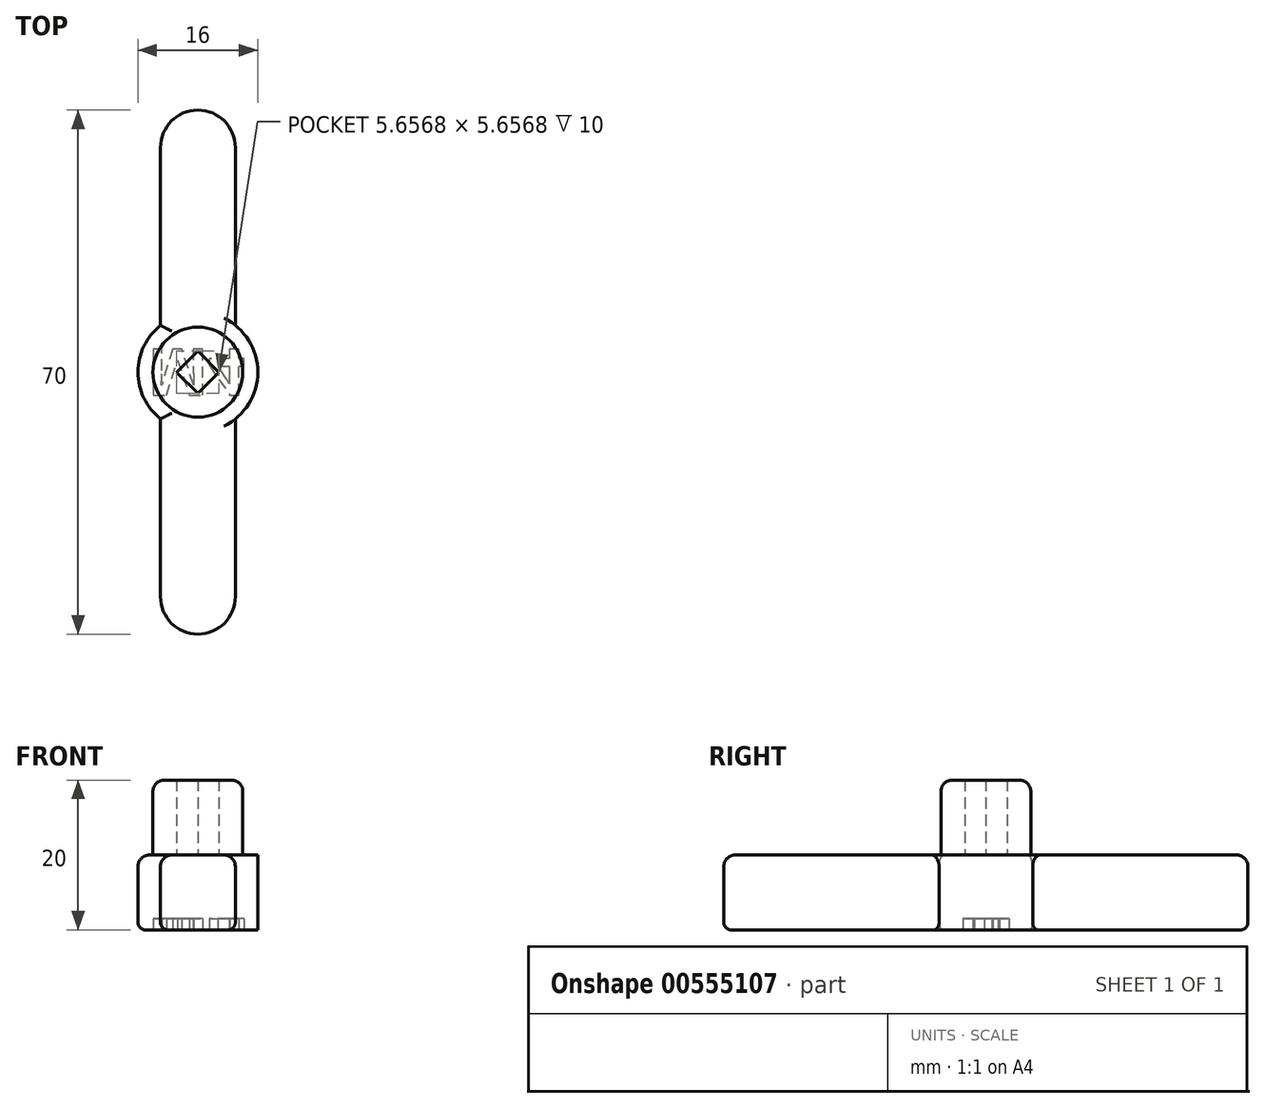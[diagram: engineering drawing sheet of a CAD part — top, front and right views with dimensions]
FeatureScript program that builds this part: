
annotation { "Feature Type Name" : "Feature", "Feature Type Description" : "" }
export const myFeature = defineFeature(function(context is Context, id is Id, definition is map)
    precondition{}
    {
        {
            var Q0;
            Q0=qCreatedBy(makeId("Top.planeOp"),FACE);
            var sketch = newSketch(context, id + "F0", { "sketchPlane" : qUnion([Q0])});
            skLineSegment(sketch, "E0.bottom", {"start": v(5, -30) * mm, "end": v(-5, -30) * mm});
            skLineSegment(sketch, "E0.top", {"start": v(5, 30) * mm, "end": v(-5, 30) * mm});
            skLineSegment(sketch, "E0.left", {"start": v(5, -30) * mm, "end": v(5, 30) * mm});
            skLineSegment(sketch, "E0.right", {"start": v(-5, -30) * mm, "end": v(-5, 30) * mm});
            skPoint(sketch, "E0.middle", {"position": v(0, 0) * mm});
            skArc(sketch, "E1", {"start": v(5, 30) * mm, "mid": v(0, 35) * mm, "end": v(-5, 30) * mm});
            skArc(sketch, "E2", {"start": v(-5, -30) * mm, "mid": v(0, -35) * mm, "end": v(5, -30) * mm});
            skCircle(sketch, "E3", {"center": v(0, 0) * mm, "radius": 8 * mm});
            skCircle(sketch, "E4", {"center": v(0, 0) * mm, "radius": 6 * mm});
            skCircle(sketch, "E5.cCircle", {"center": v(0, 0) * mm, "radius": 2.83 * mm, "construction": true});
            skLineSegment(sketch, "E5.0", {"start": v(0, -2.83) * mm, "end": v(-2.83, 0) * mm});
            skLineSegment(sketch, "E5.1", {"start": v(-2.83, 0) * mm, "end": v(0, 2.83) * mm});
            skLineSegment(sketch, "E5.2", {"start": v(0, 2.83) * mm, "end": v(2.83, 0) * mm});
            skLineSegment(sketch, "E5.3", {"start": v(2.83, 0) * mm, "end": v(0, -2.83) * mm});
            skSolve(sketch);
        }
        {
            var Q0;
            Q0=makeQuery(id+"F0.imprint","IMPRINT",FACE,{"disambiguationData":[TD([[makeQuery(id+"F0.imprint","IMPRINT",EDGE,{"derivedFrom":sQuery(id+"F0.wireOp",EDGE,"E5.0")}),1.0]])]});
            var Q1;
            {var subQ0=sQuery(id+"F0.wireOp",EDGE,"E4");var subQ1=sQuery(id+"F0.wireOp",EDGE,"E0.left");var subQ2=makeQuery(id+"F0.imprint","INTERSECT",VERTEX,{"disambiguationData":[OD(0.0)],"derivedFrom":[subQ1,subQ0]});Q1=makeQuery(id+"F0.imprint","IMPRINT",FACE,{"disambiguationData":[TD([[makeQuery(id+"F0.imprint","IMPRINT",EDGE,{"disambiguationData":[TD([[subQ2,-1.0]])],"derivedFrom":subQ1}),-1.0]])]});}
            var Q2;
            {var subQ0=sQuery(id+"F0.wireOp",EDGE,"E4");var subQ1=sQuery(id+"F0.wireOp",EDGE,"E0.right");var subQ2=makeQuery(id+"F0.imprint","INTERSECT",VERTEX,{"disambiguationData":[OD(0.0)],"derivedFrom":[subQ1,subQ0]});Q2=makeQuery(id+"F0.imprint","IMPRINT",FACE,{"disambiguationData":[TD([[makeQuery(id+"F0.imprint","IMPRINT",EDGE,{"disambiguationData":[TD([[subQ2,-1.0]])],"derivedFrom":subQ1}),1.0]])]});}
            extrude(context, id + "F1", {"entities" : qUnion([Q0, Q1, Q2]), "depth" : 20 * mm, "offsetDistance" : 25 * mm});
        }
        {
            var Q0;
            Q0=qSketchRegion(id+"F0",true);
            extrude(context, id + "F2", {"entities" : qUnion([Q0]), "operationType" : NewBodyOperationType.ADD, "depth" : 10 * mm, "offsetDistance" : 25 * mm});
        }
        {
            var Q0;
            Q0=qCreatedBy(makeId("Top.planeOp"),FACE);
            var sketch = newSketch(context, id + "F3", { "sketchPlane" : qUnion([Q0])});
            skCircle(sketch, "E6", {"center": v(0, 0) * mm, "radius": 3.52 * mm});
            skSolve(sketch);
        }
        {
            var Q0;
            Q0=makeQuery(id+"F3.imprint","IMPRINT",FACE,{"disambiguationData":[TD([[makeQuery(id+"F3.imprint","IMPRINT",EDGE,{"derivedFrom":sQuery(id+"F3.wireOp",EDGE,"E6")}),1.0]])]});
            extrude(context, id + "F4", {"entities" : qUnion([Q0]), "operationType" : NewBodyOperationType.ADD, "depth" : 10 * mm, "offsetDistance" : 25 * mm});
        }
        {
            var Q0;
            {var subQ0=sQuery(id+"F0.wireOp",EDGE,"E4");Q0=makeQuery(id+"F4.boolean.opBoolean","MERGE",FACE,{"derivedFrom":[makeQuery(id+"F2.boolean.opBoolean","MERGE",FACE,{"derivedFrom":[makeQuery(id+"F1.opExtrude","CAP_FACE",FACE,{"disambiguationData":[OSD([subQ0,sQuery(id+"F0.wireOp",EDGE,"E5.0"),sQuery(id+"F0.wireOp",EDGE,"E5.1"),sQuery(id+"F0.wireOp",EDGE,"E5.2"),sQuery(id+"F0.wireOp",EDGE,"E5.3")])],"isStart":true}),makeQuery(id+"F2.opExtrude","CAP_FACE",FACE,{"disambiguationData":[OSD([sQuery(id+"F0.wireOp",EDGE,"E0.left"),sQuery(id+"F0.wireOp",EDGE,"E0.right"),sQuery(id+"F0.wireOp",EDGE,"E1"),sQuery(id+"F0.wireOp",EDGE,"E2"),sQuery(id+"F0.wireOp",EDGE,"E3"),subQ0])],"isStart":true})]}),makeQuery(id+"F4.opExtrude","CAP_FACE",FACE,{"disambiguationData":[OSD([sQuery(id+"F3.wireOp",EDGE,"E6")])],"isStart":true})]});}
            var sketch = newSketch(context, id + "F5", { "sketchPlane" : qUnion([Q0])});
            skLineSegment(sketch, "E7.bottom", {"start": v(6.74, -3.1) * mm, "end": v(-6.74, -3.1) * mm});
            skLineSegment(sketch, "E7.top", {"start": v(6.74, 3.1) * mm, "end": v(-6.74, 3.1) * mm});
            skLineSegment(sketch, "E7.left", {"start": v(6.74, -3.1) * mm, "end": v(6.74, 3.1) * mm});
            skLineSegment(sketch, "E7.right", {"start": v(-6.74, -3.1) * mm, "end": v(-6.74, 3.1) * mm});
            skPoint(sketch, "E7.middle", {"position": v(0, 0) * mm});
            skText(sketch, "E8", { "text": "M4", "fontName": "OpenSans-Bold.ttf"});
            const initialGuessF5  = {"E8": [-0.00674, -0.0031, 1, 0, 0.00621]};
            skSetInitialGuess(sketch, initialGuessF5);
            skSolve(sketch);
        }
        {
            var Q0;
            Q0=makeQuery(id+"F5.imprint","IMPRINT",FACE,{"disambiguationData":[TD([[makeQuery(id+"F5.imprint","IMPRINT",EDGE,{"derivedFrom":sQuery(id+"F5.wireOp",EDGE,"E8.sketch_text.stroke-19")}),-1.0]])]});
            var Q1;
            Q1=makeQuery(id+"F5.imprint","IMPRINT",FACE,{"disambiguationData":[TD([[makeQuery(id+"F5.imprint","IMPRINT",EDGE,{"derivedFrom":sQuery(id+"F5.wireOp",EDGE,"E8.sketch_text.stroke-0")}),-1.0]])]});
            extrude(context, id + "F6", {"entities" : qUnion([Q0, Q1]), "operationType" : NewBodyOperationType.REMOVE, "oppositeDirection" : true, "depth" : 1.5 * mm, "offsetDistance" : 25 * mm});
        }
        {
            var Q0;
            Q0=makeQuery(id+"F1.opExtrude","CAP_EDGE",EDGE,{"disambiguationData":[OSD([sQuery(id+"F0.wireOp",EDGE,"E4")])],"isStart":false});
            fillet(context, id + "F7", {"entities" : qUnion([Q0]), "radius" : 1.5 * mm, "tangentPropagation" : true, "allowEdgeOverflow" : false});
        }
        {
            var Q0;
            Q0=makeQuery(id+"F2.opExtrude","CAP_EDGE",EDGE,{"disambiguationData":[OSD([sQuery(id+"F0.wireOp",EDGE,"E2")])],"isStart":false});
            var Q1;
            {var subQ0=sQuery(id+"F0.wireOp",EDGE,"E0.right");Q1=makeQuery(id+"F2.opExtrude","CAP_EDGE",EDGE,{"disambiguationData":[OSD([subQ0]),TDD([makeQuery(id+"F0.imprint","IMPRINT",EDGE,{"disambiguationData":[TD([[makeQuery(id+"F0.imprint","INTERSECT",VERTEX,{"disambiguationData":[OD(0.0)],"derivedFrom":[subQ0,sQuery(id+"F0.wireOp",EDGE,"E3")]}),1.0]])],"derivedFrom":subQ0})])],"isStart":false});}
            var Q2;
            {var subQ0=sQuery(id+"F0.wireOp",EDGE,"E3");var subQ1=sQuery(id+"F0.wireOp",EDGE,"E0.right");Q2=makeQuery(id+"F2.opExtrude","CAP_EDGE",EDGE,{"disambiguationData":[OSD([subQ0]),TDD([makeQuery(id+"F0.imprint","IMPRINT",EDGE,{"disambiguationData":[TD([[makeQuery(id+"F0.imprint","INTERSECT",VERTEX,{"disambiguationData":[OD(0.0)],"derivedFrom":[subQ1,subQ0]}),1.0]])],"derivedFrom":subQ0})])],"isStart":false});}
            var Q3;
            {var subQ0=sQuery(id+"F0.wireOp",EDGE,"E0.right");Q3=makeQuery(id+"F2.opExtrude","CAP_EDGE",EDGE,{"disambiguationData":[OSD([subQ0]),TDD([makeQuery(id+"F0.imprint","IMPRINT",EDGE,{"disambiguationData":[TD([[makeQuery(id+"F0.imprint","INTERSECT",VERTEX,{"disambiguationData":[OD(1.0)],"derivedFrom":[subQ0,sQuery(id+"F0.wireOp",EDGE,"E3")]}),-1.0]])],"derivedFrom":subQ0})])],"isStart":false});}
            var Q4;
            Q4=makeQuery(id+"F2.opExtrude","CAP_EDGE",EDGE,{"disambiguationData":[OSD([sQuery(id+"F0.wireOp",EDGE,"E1")])],"isStart":false});
            var Q5;
            {var subQ0=sQuery(id+"F0.wireOp",EDGE,"E0.left");Q5=makeQuery(id+"F2.opExtrude","CAP_EDGE",EDGE,{"disambiguationData":[OSD([subQ0]),TDD([makeQuery(id+"F0.imprint","IMPRINT",EDGE,{"disambiguationData":[TD([[makeQuery(id+"F0.imprint","INTERSECT",VERTEX,{"disambiguationData":[OD(1.0)],"derivedFrom":[subQ0,sQuery(id+"F0.wireOp",EDGE,"E3")]}),-1.0]])],"derivedFrom":subQ0})])],"isStart":false});}
            var Q6;
            {var subQ0=sQuery(id+"F0.wireOp",EDGE,"E3");var subQ1=sQuery(id+"F0.wireOp",EDGE,"E0.left");Q6=makeQuery(id+"F2.opExtrude","CAP_EDGE",EDGE,{"disambiguationData":[OSD([subQ0]),TDD([makeQuery(id+"F0.imprint","IMPRINT",EDGE,{"disambiguationData":[TD([[makeQuery(id+"F0.imprint","INTERSECT",VERTEX,{"disambiguationData":[OD(0.0)],"derivedFrom":[subQ1,subQ0]}),-1.0]])],"derivedFrom":subQ0})])],"isStart":false});}
            var Q7;
            {var subQ0=sQuery(id+"F0.wireOp",EDGE,"E0.left");Q7=makeQuery(id+"F2.opExtrude","CAP_EDGE",EDGE,{"disambiguationData":[OSD([subQ0]),TDD([makeQuery(id+"F0.imprint","IMPRINT",EDGE,{"disambiguationData":[TD([[makeQuery(id+"F0.imprint","INTERSECT",VERTEX,{"disambiguationData":[OD(0.0)],"derivedFrom":[subQ0,sQuery(id+"F0.wireOp",EDGE,"E3")]}),1.0]])],"derivedFrom":subQ0})])],"isStart":false});}
            fillet(context, id + "F8", {"entities" : qUnion([Q0, Q1, Q2, Q3, Q4, Q5, Q6, Q7]), "radius" : 1.5 * mm, "tangentPropagation" : true, "allowEdgeOverflow" : false});
        }
        {
            var Q0;
            {var subQ0=sQuery(id+"F0.wireOp",EDGE,"E0.left");Q0=makeQuery(id+"F2.opExtrude","CAP_EDGE",EDGE,{"disambiguationData":[OSD([subQ0]),TDD([makeQuery(id+"F0.imprint","IMPRINT",EDGE,{"disambiguationData":[TD([[makeQuery(id+"F0.imprint","INTERSECT",VERTEX,{"disambiguationData":[OD(0.0)],"derivedFrom":[subQ0,sQuery(id+"F0.wireOp",EDGE,"E3")]}),1.0]])],"derivedFrom":subQ0})])],"isStart":true});}
            var Q1;
            Q1=makeQuery(id+"F2.opExtrude","CAP_EDGE",EDGE,{"disambiguationData":[OSD([sQuery(id+"F0.wireOp",EDGE,"E2")])],"isStart":true});
            var Q2;
            {var subQ0=sQuery(id+"F0.wireOp",EDGE,"E3");var subQ1=sQuery(id+"F0.wireOp",EDGE,"E0.right");Q2=makeQuery(id+"F2.opExtrude","CAP_EDGE",EDGE,{"disambiguationData":[OSD([subQ0]),TDD([makeQuery(id+"F0.imprint","IMPRINT",EDGE,{"disambiguationData":[TD([[makeQuery(id+"F0.imprint","INTERSECT",VERTEX,{"disambiguationData":[OD(0.0)],"derivedFrom":[subQ1,subQ0]}),1.0]])],"derivedFrom":subQ0})])],"isStart":true});}
            var Q3;
            {var subQ0=sQuery(id+"F0.wireOp",EDGE,"E0.right");Q3=makeQuery(id+"F2.opExtrude","CAP_EDGE",EDGE,{"disambiguationData":[OSD([subQ0]),TDD([makeQuery(id+"F0.imprint","IMPRINT",EDGE,{"disambiguationData":[TD([[makeQuery(id+"F0.imprint","INTERSECT",VERTEX,{"disambiguationData":[OD(0.0)],"derivedFrom":[subQ0,sQuery(id+"F0.wireOp",EDGE,"E3")]}),1.0]])],"derivedFrom":subQ0})])],"isStart":true});}
            var Q4;
            {var subQ0=sQuery(id+"F0.wireOp",EDGE,"E0.left");Q4=makeQuery(id+"F2.opExtrude","CAP_EDGE",EDGE,{"disambiguationData":[OSD([subQ0]),TDD([makeQuery(id+"F0.imprint","IMPRINT",EDGE,{"disambiguationData":[TD([[makeQuery(id+"F0.imprint","INTERSECT",VERTEX,{"disambiguationData":[OD(1.0)],"derivedFrom":[subQ0,sQuery(id+"F0.wireOp",EDGE,"E3")]}),-1.0]])],"derivedFrom":subQ0})])],"isStart":true});}
            var Q5;
            {var subQ0=sQuery(id+"F0.wireOp",EDGE,"E0.right");Q5=makeQuery(id+"F2.opExtrude","CAP_EDGE",EDGE,{"disambiguationData":[OSD([subQ0]),TDD([makeQuery(id+"F0.imprint","IMPRINT",EDGE,{"disambiguationData":[TD([[makeQuery(id+"F0.imprint","INTERSECT",VERTEX,{"disambiguationData":[OD(1.0)],"derivedFrom":[subQ0,sQuery(id+"F0.wireOp",EDGE,"E3")]}),-1.0]])],"derivedFrom":subQ0})])],"isStart":true});}
            var Q6;
            Q6=makeQuery(id+"F2.opExtrude","CAP_EDGE",EDGE,{"disambiguationData":[OSD([sQuery(id+"F0.wireOp",EDGE,"E1")])],"isStart":true});
            var Q7;
            {var subQ0=sQuery(id+"F0.wireOp",EDGE,"E3");var subQ1=sQuery(id+"F0.wireOp",EDGE,"E0.left");Q7=makeQuery(id+"F2.opExtrude","CAP_EDGE",EDGE,{"disambiguationData":[OSD([subQ0]),TDD([makeQuery(id+"F0.imprint","IMPRINT",EDGE,{"disambiguationData":[TD([[makeQuery(id+"F0.imprint","INTERSECT",VERTEX,{"disambiguationData":[OD(0.0)],"derivedFrom":[subQ1,subQ0]}),-1.0]])],"derivedFrom":subQ0})])],"isStart":true});}
            fillet(context, id + "F9", {"entities" : qUnion([Q0, Q1, Q2, Q3, Q4, Q5, Q6, Q7]), "radius" : 1 * mm, "tangentPropagation" : true, "allowEdgeOverflow" : false});
        }
    });
